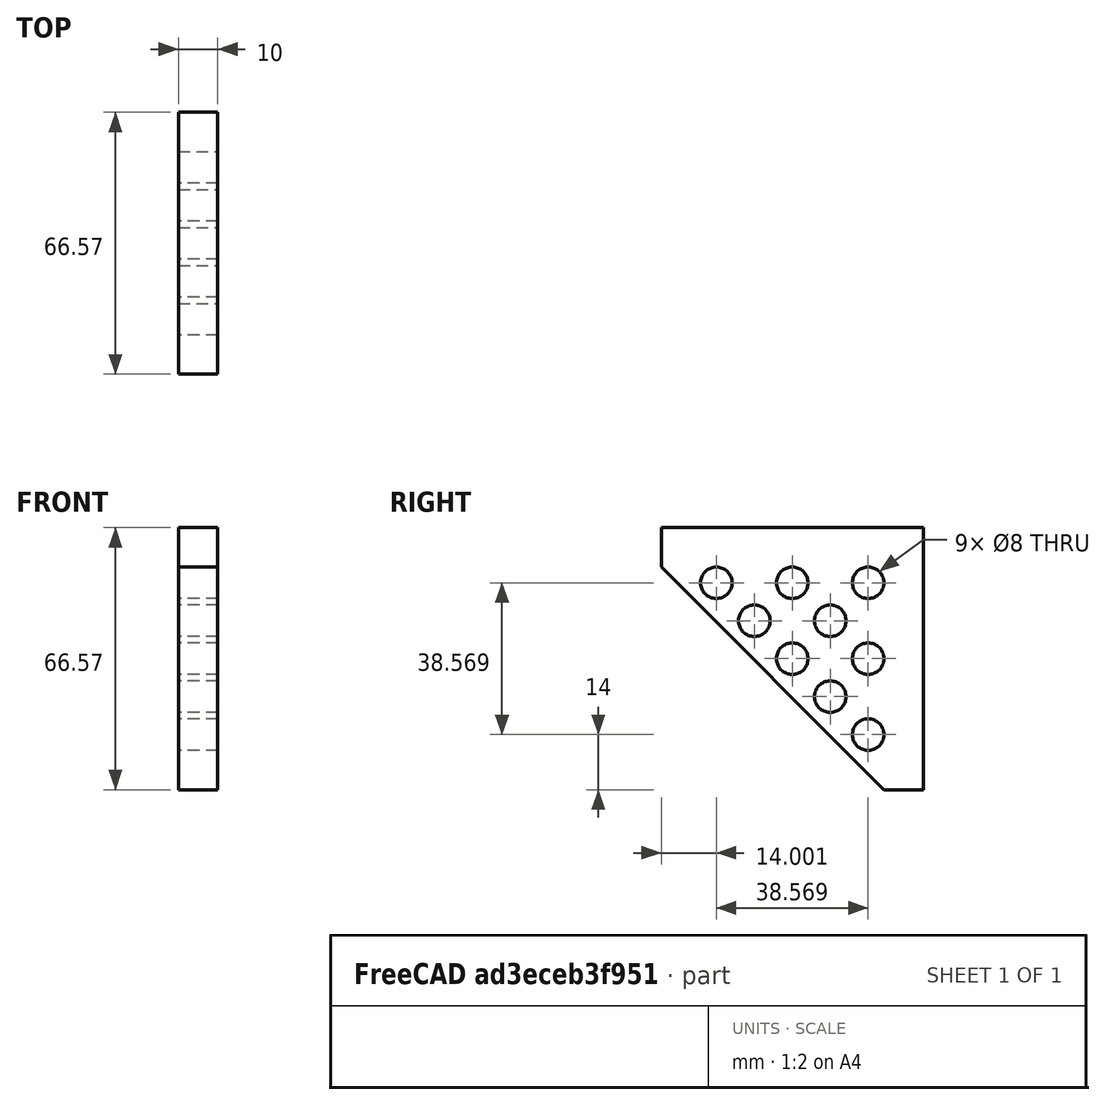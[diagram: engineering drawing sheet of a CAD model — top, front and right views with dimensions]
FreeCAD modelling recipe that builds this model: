
FCSTD DOCUMENT  (FreeCAD 0.18R4 (GitTag))
Label: pc_fan_side
License: All rights reserved
LicenseURL: http://en.wikipedia.org/wiki/All_rights_reserved
objects: Sketcher::SketchObject×1, PartDesign::Pad×1, PartDesign::Body×1
note: 4 computed .brp shape members not serialized (recipe doc carries the construction recipe); baked Part::Feature solids carry a one-line shape summary decoded from their .brp

FEATURE [Sketcher::SketchObject] Sketch
  MapMode = 5
  Placement = pos=(0,0,0) rot=(0.57735,0.57735,0.57735;2.0944rad)
  Support = -> [YZ_Plane]
  sketch-geometry (14):
    g0: LineSegment StartX=0 StartY=7.1e-15 StartZ=0 EndX=0 EndY=66.5685 EndZ=0
    g1: LineSegment StartX=0 StartY=66.5685 StartZ=0 EndX=-66.5685 EndY=66.5685 EndZ=0
    g2: LineSegment StartX=-66.5685 StartY=66.5685 StartZ=0 EndX=-66.5685 EndY=56.5685 EndZ=0
    g3: LineSegment StartX=0 StartY=7.1e-15 StartZ=0 EndX=-10 EndY=7.1e-15 EndZ=0
    g4: LineSegment StartX=-66.5685 StartY=56.5685 StartZ=0 EndX=-10 EndY=7.1e-15 EndZ=0
    g5: Circle CenterX=-14 CenterY=52.5685 CenterZ=0 NormalX=0 NormalY=0 NormalZ=1 AngleXU=0 Radius=4
    g6: Circle CenterX=-52.5685 CenterY=52.5685 CenterZ=0 NormalX=0 NormalY=0 NormalZ=1 AngleXU=0 Radius=4
    g7: Circle CenterX=-14 CenterY=14 CenterZ=0 NormalX=0 NormalY=0 NormalZ=1 AngleXU=0 Radius=4
    g8: Circle CenterX=-33.285 CenterY=52.5685 CenterZ=0 NormalX=0 NormalY=0 NormalZ=1 AngleXU=0 Radius=4
    g9: Circle CenterX=-14 CenterY=33.285 CenterZ=0 NormalX=0 NormalY=0 NormalZ=1 AngleXU=0 Radius=4
    g10: Circle CenterX=-33.285 CenterY=33.285 CenterZ=0 NormalX=0 NormalY=0 NormalZ=1 AngleXU=0 Radius=4
    g11: Circle CenterX=-42.9275 CenterY=42.9275 CenterZ=0 NormalX=0 NormalY=0 NormalZ=1 AngleXU=0 Radius=4
    g12: Circle CenterX=-23.6425 CenterY=42.9275 CenterZ=0 NormalX=0 NormalY=0 NormalZ=1 AngleXU=0 Radius=4
    g13: Circle CenterX=-23.6425 CenterY=23.6425 CenterZ=0 NormalX=0 NormalY=0 NormalZ=1 AngleXU=0 Radius=4
  constraints (41):
    c: Coincident(g1,g0)
    c: Coincident(g1,g2)
    c: Vertical(g0)
    c: Vertical(g2)
    c: Horizontal(g1)
    c: DistanceY(g2,g2) = 10
    c: Coincident(g3,g0)
    c: Coincident(g0,g-1)
    c: Horizontal(g3)
    c: DistanceX(g3,g3) = 10
    c: Coincident(g4,g3)
    c: Angle(g-1,g4) = 2.35619
    c: Distance(g2,g3) = 80
    c: Coincident(g2,g4)
    c: Diameter(g5) = 8
    c: Diameter(g6) = 8
    c: Diameter(g7) = 8
    c: DistanceX(g5,g0) = 14
    c: DistanceY(g5,g0) = 14
    c: DistanceY(g0,g7) = 14
    c: DistanceX(g1,g6) = 14
    c: Diameter(g8) = 8
    c: Diameter(g9) = 8
    c: Diameter(g10) = 8
    c: DistanceX(g10,g8) = 0
    c: DistanceY(g9,g10) = 0
    c: DistanceX(g7,g9) = 0
    c: DistanceX(g5,g9) = 0
    c: DistanceY(g8,g6) = 0
    c: DistanceY(g8,g5) = 0
    c: Diameter(g12) = 8
    c: Diameter(g11) = 8
    c: Diameter(g13) = 8
    c: DistanceX(g12,g5) = 9.6425
    c: DistanceX(g8,g12) = 9.6425
    c: DistanceX(g11,g8) = 9.6425
    c: DistanceY(g7,g13) = 9.6425
    c: DistanceY(g13,g9) = 9.6425
    c: DistanceY(g9,g12) = 9.6425
    c: DistanceX(g12,g13) = 0
    c: DistanceY(g12,g11) = 0
FEATURE [PartDesign::Pad] Pad
  Length = 10
  Length2 = 100
  Placement = pos=(0,0,0) rot=(0.57735,0.57735,0.57735;2.0944rad)
  Profile = -> Sketch
  Type = 0
FEATURE [PartDesign::Body] Body
  Group = -> [Sketch,Pad]
  Origin = -> Origin
  Tip = -> Pad
